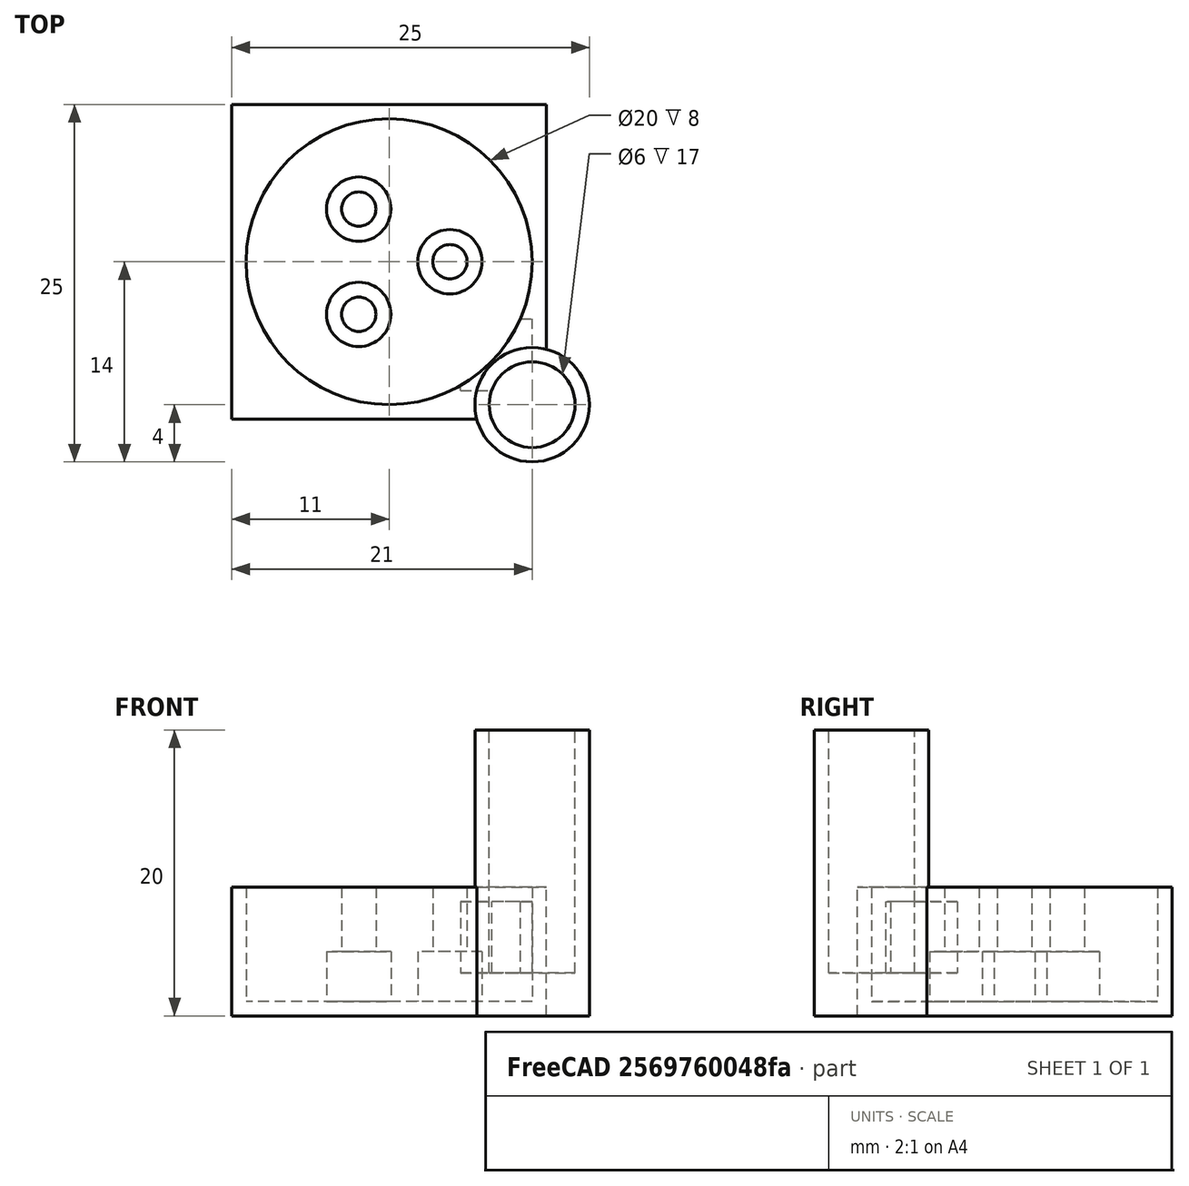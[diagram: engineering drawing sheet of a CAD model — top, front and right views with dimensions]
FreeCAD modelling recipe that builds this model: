
FCSTD DOCUMENT  (FreeCAD 0.17R13509 (Git))
Label: insert
License: All rights reserved
LicenseURL: http://en.wikipedia.org/wiki/All_rights_reserved
objects: Part::Cylinder×7, Part::MultiFuse×4, Part::Cut×3, Part::Box×2, Part::FeaturePython×1
note: 17 computed .brp shape members not serialized (recipe doc carries the construction recipe); baked Part::Feature solids carry a one-line shape summary decoded from their .brp

FEATURE [Part::Cylinder] Cylinder153  label="Body"
  Angle = 360
  AttacherType = Attacher::AttachEngine3D
  Height = 9
  Placement = pos=(0,0,-1) rot=(0,0,1;0rad)
  Radius = 10
FEATURE [Part::Cylinder] Cylinder147  label="ThreadedSection"
  Angle = 360
  AttacherType = Attacher::AttachEngine3D
  Height = 1
  Placement = pos=(0,0,4.5) rot=(0,0,1;0rad)
  Radius = 1
FEATURE [Part::Cylinder] Cylinder156  label="BottomWireOutlet"
  Angle = 360
  AttacherType = Attacher::AttachEngine3D
  Height = 14
  Placement = pos=(0,0,-7) rot=(0,0,1;0rad)
  Radius = 1.2
FEATURE [Part::Cylinder] Cylinder157  label="SealSubtraction"
  Angle = 360
  AttacherType = Attacher::AttachEngine3D
  Height = 7
  Placement = pos=(0,0,4.5) rot=(0,0,1;0rad)
  Radius = 2.25
FEATURE [Part::MultiFuse] Fusion
  Placement = pos=(4.25,0,0) rot=(0,0,1;0rad)
  Shapes = -> [Cylinder147,Cylinder157,Cylinder156]
FEATURE [Part::FeaturePython] Array  label="SealArray"  # Draft array (typed FeaturePython)
  Angle = 360
  ArrayType = 1
  Axis = (0,0,1)
  Base = -> Fusion
  Center = (0,0,0)
  Fuse = false
  IntervalAxis = (0,0,0)
  IntervalX = (1,0,0)
  IntervalY = (0,1,0)
  IntervalZ = (0,0,0)
  NumberPolar = 3
  NumberX = 2
  NumberY = 2
  NumberZ = 1
FEATURE [Part::Cut] Cut
  Base = -> Cylinder153
  Placement = pos=(0,0,9) rot=(1,0,0;3.14159rad)
  Tool = -> Array
FEATURE [Part::Cylinder] Cylinder158  label="Cylinder001"
  Angle = 360
  AttacherType = Attacher::AttachEngine3D
  Height = 23
  Placement = pos=(10,-10,3) rot=(0,0,1;0rad)
  Radius = 3
FEATURE [Part::Box] Box  label="Cube"
  AttacherType = Attacher::AttachEngine3D
  Height = 9
  Length = 22
  Placement = pos=(-11,-11,0) rot=(0,0,1;0rad)
  Width = 22
FEATURE [Part::Cylinder] Cylinder159  label="Cylinder002"
  Angle = 360
  AttacherType = Attacher::AttachEngine3D
  Height = 20
  Placement = pos=(10,-10,0) rot=(0,0,1;0rad)
  Radius = 4
FEATURE [Part::Cylinder] Cylinder
  Angle = 360
  AttacherType = Attacher::AttachEngine3D
  Height = 10
  Placement = pos=(0,0,6) rot=(0,0,1;0rad)
  Radius = 1
FEATURE [Part::MultiFuse] Fusion001
  Shapes = -> [Cylinder,Cylinder158]
FEATURE [Part::MultiFuse] Fusion002
  Shapes = -> [Box,Cylinder159]
FEATURE [Part::MultiFuse] Fusion003
  Shapes = -> [Fusion001,Cut]
FEATURE [Part::Cut] Cut001
  Base = -> Fusion002
  Tool = -> Fusion003
FEATURE [Part::Box] Box001  label="Cube001"
  AttacherType = Attacher::AttachEngine3D
  Height = 5
  Length = 5
  Placement = pos=(5,-9,3) rot=(0,0,1;0rad)
  Width = 5
FEATURE [Part::Cut] Cut002
  Base = -> Cut001
  Tool = -> Box001
